# Revit family: Ниппель переходной для Н-образного фитинга R3-4 Евроконус R1-2
name_source: partatom
category: Соединительные детали трубопроводов
revit_build: Autodesk Revit 2017 (Build: 20160225_1515(x64)
units: mm (PartAtom-declared; Revit-internal decimal feet)

## family parameters
Всегда вертикально = Да
На основе рабочей плоскости = Нет
Общий = Да
При загрузке вырезать с полостями = Нет
Размер круглого соединителя = Использовать радиус
Тип детали = Переход

## types (1)
- Нипель переходной для Н-образного фитинга R3/4 Евроконус R1/2
    ADSK_Единица измерения = шт
    ADSK_Завод-изготовитель = Sanext
    ADSK_Код изделия = 4969
    ADSK_Масса = 0
    ADSK_Наименование = Нипель переходной для Н-образного фитинга R3/4 Евроконус R1/2
    DN1 = 25 мм
    DN2 = 20 мм
    R1 = 13 мм
    R2 = 10 мм
    URL = http://sanext.ru
    h = 20 мм
    Изготовитель = Sanext
    Материал фитинга = DZR латунь
    Разработчик = ООО ПРОРУБИМ
    Разработчик (телефон) = +7(495)649-85-43
    Разработчик модели (URL) = http://prorubim.com
